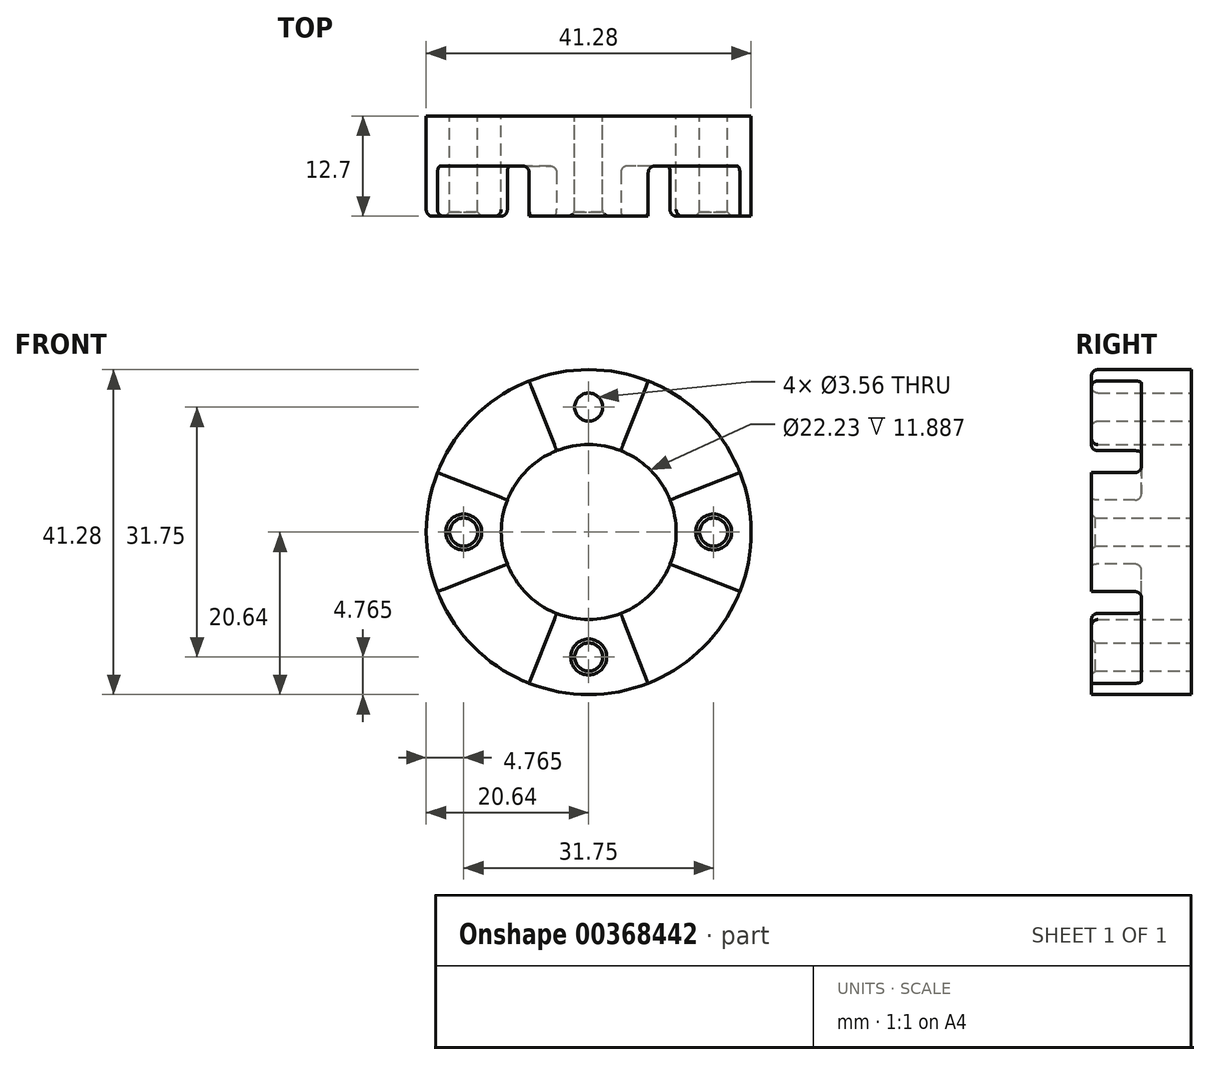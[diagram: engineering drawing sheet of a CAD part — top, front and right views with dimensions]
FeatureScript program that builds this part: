
annotation { "Feature Type Name" : "Feature", "Feature Type Description" : "" }
export const myFeature = defineFeature(function(context is Context, id is Id, definition is map)
    precondition{}
    {
        {
            var Q0;
            Q0=qCreatedBy(makeId("Front.planeOp"),FACE);
            var sketch = newSketch(context, id + "F0", { "sketchPlane" : qUnion([Q0]), "disableImprinting" : false});
            skCircle(sketch, "E0", {"center": v(0, 0) * mm, "radius": 20.64 * mm});
            skCircle(sketch, "E1", {"center": v(0, 0) * mm, "radius": 11.11 * mm});
            skLineSegment(sketch, "E2", {"start": v(0, 20.64) * mm, "end": v(0, -40.4) * mm, "construction": true});
            skLineSegment(sketch, "E3", {"start": v(-50.78, 0) * mm, "end": v(44.22, 0) * mm, "construction": true});
            skCircle(sketch, "E4", {"center": v(0, 15.88) * mm, "radius": 1.78 * mm});
            skPoint(sketch, "E5.orphan", {"position": v(0, 46.95) * mm});
            skCircle(sketch, "E6.1.0", {"center": v(-15.88, 0) * mm, "radius": 1.78 * mm});
            skCircle(sketch, "E6.2.0", {"center": v(0, -15.88) * mm, "radius": 1.78 * mm});
            skCircle(sketch, "E6.3.0", {"center": v(15.88, 0) * mm, "radius": 1.78 * mm});
            skSolve(sketch);
        }
        {
            var Q0;
            Q0=makeQuery(id+"F0.imprint","IMPRINT",FACE,{"disambiguationData":[TD([[makeQuery(id+"F0.imprint","IMPRINT",EDGE,{"derivedFrom":sQuery(id+"F0.wireOp",EDGE,"E0")}),1.0]])]});
            extrude(context, id + "F1", {"entities" : qUnion([Q0]), "flatOperationType" : FlatOperationType.REMOVE, "offsetDistance" : 25.4 * mm, "depth" : 12.7 * mm, "domain" : OperationDomain.MODEL});
        }
        {
            var Q0;
            Q0=makeQuery(id+"F1.opExtrude","CAP_EDGE",EDGE,{"disambiguationData":[OSD([sQuery(id+"F0.wireOp",EDGE,"E6.1.0")])],"isStart":false});
            var Q1;
            Q1=makeQuery(id+"F1.opExtrude","CAP_EDGE",EDGE,{"disambiguationData":[OSD([sQuery(id+"F0.wireOp",EDGE,"E4")])],"isStart":false});
            var Q2;
            Q2=makeQuery(id+"F1.opExtrude","CAP_EDGE",EDGE,{"disambiguationData":[OSD([sQuery(id+"F0.wireOp",EDGE,"E6.3.0")])],"isStart":false});
            var Q3;
            Q3=makeQuery(id+"F1.opExtrude","CAP_EDGE",EDGE,{"disambiguationData":[OSD([sQuery(id+"F0.wireOp",EDGE,"E6.2.0")])],"isStart":false});
            chamfer(context, id + "F2", {"entities" : qUnion([Q0, Q1, Q2, Q3]), "width" : 0.5 * mm, "tangentPropagation" : true});
        }
        {
            var Q0;
            Q0=makeQuery(id+"F1.opExtrude","CAP_FACE",FACE,{"disambiguationData":[OSD([sQuery(id+"F0.wireOp",EDGE,"E0"),sQuery(id+"F0.wireOp",EDGE,"E1"),sQuery(id+"F0.wireOp",EDGE,"E4"),sQuery(id+"F0.wireOp",EDGE,"E6.1.0"),sQuery(id+"F0.wireOp",EDGE,"E6.2.0"),sQuery(id+"F0.wireOp",EDGE,"E6.3.0")])],"isStart":false});
            var sketch = newSketch(context, id + "F3", { "sketchPlane" : qUnion([Q0]), "disableImprinting" : false});
            skLineSegment(sketch, "E7", {"start": v(19.2, 7.56) * mm, "end": v(0, 0) * mm});
            skLineSegment(sketch, "E8", {"start": v(19.2, -7.56) * mm, "end": v(0, 0) * mm});
            skLineSegment(sketch, "E9", {"start": v(7.56, 19.2) * mm, "end": v(0, 0) * mm});
            skLineSegment(sketch, "E10", {"start": v(0, 0) * mm, "end": v(7.56, -19.2) * mm});
            skLineSegment(sketch, "E11", {"start": v(0, 0) * mm, "end": v(-7.56, -19.2) * mm});
            skLineSegment(sketch, "E12", {"start": v(0, 0) * mm, "end": v(-19.2, -7.56) * mm});
            skLineSegment(sketch, "E13", {"start": v(0, 0) * mm, "end": v(-19.2, 7.56) * mm});
            skLineSegment(sketch, "E14", {"start": v(0, 0) * mm, "end": v(-7.56, 19.2) * mm});
            skSolve(sketch);
        }
        {
            var Q0;
            {var subQ0=sQuery(id+"F3.wireOp",EDGE,"E7");var subQ1=makeQuery(id+"F1.opExtrude","CAP_EDGE",EDGE,{"disambiguationData":[OSD([sQuery(id+"F0.wireOp",EDGE,"E0")])],"isStart":false});var subQ2=makeQuery(id+"F3.imprint","INTERSECT",VERTEX,{"derivedFrom":[subQ1,subQ0]});Q0=makeQuery(id+"F3.imprint","IMPRINT",FACE,{"disambiguationData":[TD([[makeQuery(id+"F3.imprint","IMPRINT",EDGE,{"disambiguationData":[TD([[subQ2,-1.0]])],"derivedFrom":subQ0}),-1.0]])]});}
            var Q1;
            {var subQ0=sQuery(id+"F3.wireOp",EDGE,"E8");var subQ1=makeQuery(id+"F1.opExtrude","CAP_EDGE",EDGE,{"disambiguationData":[OSD([sQuery(id+"F0.wireOp",EDGE,"E0")])],"isStart":false});var subQ2=makeQuery(id+"F3.imprint","INTERSECT",VERTEX,{"derivedFrom":[subQ1,subQ0]});Q1=makeQuery(id+"F3.imprint","IMPRINT",FACE,{"disambiguationData":[TD([[makeQuery(id+"F3.imprint","IMPRINT",EDGE,{"disambiguationData":[TD([[subQ2,-1.0]])],"derivedFrom":subQ0}),1.0]])]});}
            var Q2;
            {var subQ0=sQuery(id+"F3.wireOp",EDGE,"E11");var subQ1=makeQuery(id+"F1.opExtrude","CAP_EDGE",EDGE,{"disambiguationData":[OSD([sQuery(id+"F0.wireOp",EDGE,"E0")])],"isStart":false});var subQ2=makeQuery(id+"F3.imprint","INTERSECT",VERTEX,{"derivedFrom":[subQ1,subQ0]});Q2=makeQuery(id+"F3.imprint","IMPRINT",FACE,{"disambiguationData":[TD([[makeQuery(id+"F3.imprint","IMPRINT",EDGE,{"disambiguationData":[TD([[subQ2,1.0]])],"derivedFrom":subQ0}),-1.0]])]});}
            var Q3;
            {var subQ0=sQuery(id+"F3.wireOp",EDGE,"E13");var subQ1=makeQuery(id+"F1.opExtrude","CAP_EDGE",EDGE,{"disambiguationData":[OSD([sQuery(id+"F0.wireOp",EDGE,"E0")])],"isStart":false});var subQ2=makeQuery(id+"F3.imprint","INTERSECT",VERTEX,{"derivedFrom":[subQ1,subQ0]});Q3=makeQuery(id+"F3.imprint","IMPRINT",FACE,{"disambiguationData":[TD([[makeQuery(id+"F3.imprint","IMPRINT",EDGE,{"disambiguationData":[TD([[subQ2,1.0]])],"derivedFrom":subQ0}),-1.0]])]});}
            extrude(context, id + "F4", {"entities" : qUnion([Q0, Q1, Q2, Q3]), "operationType" : NewBodyOperationType.REMOVE, "oppositeDirection" : true, "depth" : 6.35 * mm});
        }
        {
            var Q0;
            Q0=makeQuery(id+"F4.boolean.opBoolean","COPY",EDGE,{"derivedFrom":makeQuery(id+"F4.opExtrude","CAP_EDGE",EDGE,{"disambiguationData":[OSD([sQuery(id+"F3.wireOp",EDGE,"E7")])],"isStart":true})});
            var Q1;
            Q1=makeQuery(id+"F4.boolean.opBoolean","COPY",EDGE,{"derivedFrom":makeQuery(id+"F4.opExtrude","CAP_EDGE",EDGE,{"disambiguationData":[OSD([sQuery(id+"F3.wireOp",EDGE,"E7")])],"isStart":false})});
            var Q2;
            Q2=makeQuery(id+"F4.boolean.opBoolean","COPY",EDGE,{"derivedFrom":makeQuery(id+"F4.opExtrude","CAP_EDGE",EDGE,{"disambiguationData":[OSD([sQuery(id+"F3.wireOp",EDGE,"E9")])],"isStart":true})});
            var Q3;
            Q3=makeQuery(id+"F4.boolean.opBoolean","COPY",EDGE,{"derivedFrom":makeQuery(id+"F4.opExtrude","CAP_EDGE",EDGE,{"disambiguationData":[OSD([sQuery(id+"F3.wireOp",EDGE,"E8")])],"isStart":true})});
            var Q4;
            Q4=makeQuery(id+"F4.boolean.opBoolean","COPY",EDGE,{"derivedFrom":makeQuery(id+"F4.opExtrude","CAP_EDGE",EDGE,{"disambiguationData":[OSD([sQuery(id+"F3.wireOp",EDGE,"E10")])],"isStart":true})});
            var Q5;
            Q5=makeQuery(id+"F4.boolean.opBoolean","COPY",EDGE,{"derivedFrom":makeQuery(id+"F4.opExtrude","CAP_EDGE",EDGE,{"disambiguationData":[OSD([sQuery(id+"F3.wireOp",EDGE,"E10")])],"isStart":false})});
            var Q6;
            Q6=makeQuery(id+"F4.boolean.opBoolean","COPY",EDGE,{"derivedFrom":makeQuery(id+"F4.opExtrude","CAP_EDGE",EDGE,{"disambiguationData":[OSD([sQuery(id+"F3.wireOp",EDGE,"E11")])],"isStart":true})});
            var Q7;
            Q7=makeQuery(id+"F4.boolean.opBoolean","COPY",EDGE,{"derivedFrom":makeQuery(id+"F4.opExtrude","CAP_EDGE",EDGE,{"disambiguationData":[OSD([sQuery(id+"F3.wireOp",EDGE,"E13")])],"isStart":true})});
            var Q8;
            Q8=makeQuery(id+"F4.boolean.opBoolean","COPY",EDGE,{"derivedFrom":makeQuery(id+"F4.opExtrude","CAP_EDGE",EDGE,{"disambiguationData":[OSD([sQuery(id+"F3.wireOp",EDGE,"E13")])],"isStart":false})});
            var Q9;
            Q9=makeQuery(id+"F4.boolean.opBoolean","COPY",EDGE,{"derivedFrom":makeQuery(id+"F4.opExtrude","CAP_EDGE",EDGE,{"disambiguationData":[OSD([sQuery(id+"F3.wireOp",EDGE,"E14")])],"isStart":true})});
            var Q10;
            Q10=makeQuery(id+"F4.boolean.opBoolean","COPY",EDGE,{"derivedFrom":makeQuery(id+"F4.opExtrude","CAP_EDGE",EDGE,{"disambiguationData":[OSD([sQuery(id+"F3.wireOp",EDGE,"E11")])],"isStart":false})});
            var Q11;
            Q11=makeQuery(id+"F4.boolean.opBoolean","COPY",EDGE,{"derivedFrom":makeQuery(id+"F4.opExtrude","CAP_EDGE",EDGE,{"disambiguationData":[OSD([sQuery(id+"F3.wireOp",EDGE,"E8")])],"isStart":false})});
            var Q12;
            Q12=makeQuery(id+"F4.boolean.opBoolean","COPY",EDGE,{"derivedFrom":makeQuery(id+"F4.opExtrude","CAP_EDGE",EDGE,{"disambiguationData":[OSD([sQuery(id+"F3.wireOp",EDGE,"E12")])],"isStart":false})});
            var Q13;
            Q13=makeQuery(id+"F4.boolean.opBoolean","COPY",EDGE,{"derivedFrom":makeQuery(id+"F4.opExtrude","CAP_EDGE",EDGE,{"disambiguationData":[OSD([sQuery(id+"F3.wireOp",EDGE,"E12")])],"isStart":true})});
            var Q14;
            Q14=makeQuery(id+"F4.boolean.opBoolean","COPY",EDGE,{"derivedFrom":makeQuery(id+"F4.opExtrude","CAP_EDGE",EDGE,{"disambiguationData":[OSD([sQuery(id+"F3.wireOp",EDGE,"E14")])],"isStart":false})});
            var Q15;
            Q15=makeQuery(id+"F4.boolean.opBoolean","COPY",EDGE,{"derivedFrom":makeQuery(id+"F4.opExtrude","CAP_EDGE",EDGE,{"disambiguationData":[OSD([sQuery(id+"F3.wireOp",EDGE,"E9")])],"isStart":false})});
            var Q16;
            {var subQ0=sQuery(id+"F0.wireOp",EDGE,"E1");Q16=makeQuery(id+"F4.boolean.opBoolean","SPLIT",EDGE,{"disambiguationData":[TD([makeQuery(id+"F4.opExtrude","SWEPT_FACE",FACE,{"disambiguationData":[OSD([sQuery(id+"F3.wireOp",EDGE,"E7")])]})])],"derivedFrom":makeQuery(id+"F1.opExtrude","CAP_EDGE",EDGE,{"disambiguationData":[OSD([subQ0])],"isStart":false})});}
            var Q17;
            {var subQ0=sQuery(id+"F0.wireOp",EDGE,"E1");Q17=makeQuery(id+"F4.boolean.opBoolean","SPLIT",EDGE,{"disambiguationData":[TD([makeQuery(id+"F4.opExtrude","SWEPT_FACE",FACE,{"disambiguationData":[OSD([sQuery(id+"F3.wireOp",EDGE,"E10")])]})])],"derivedFrom":makeQuery(id+"F1.opExtrude","CAP_EDGE",EDGE,{"disambiguationData":[OSD([subQ0])],"isStart":false})});}
            var Q18;
            {var subQ0=sQuery(id+"F0.wireOp",EDGE,"E1");Q18=makeQuery(id+"F4.boolean.opBoolean","SPLIT",EDGE,{"disambiguationData":[TD([makeQuery(id+"F4.opExtrude","SWEPT_FACE",FACE,{"disambiguationData":[OSD([sQuery(id+"F3.wireOp",EDGE,"E12")])]})])],"derivedFrom":makeQuery(id+"F1.opExtrude","CAP_EDGE",EDGE,{"disambiguationData":[OSD([subQ0])],"isStart":false})});}
            var Q19;
            {var subQ0=sQuery(id+"F0.wireOp",EDGE,"E1");Q19=makeQuery(id+"F4.boolean.opBoolean","SPLIT",EDGE,{"disambiguationData":[TD([makeQuery(id+"F4.opExtrude","SWEPT_FACE",FACE,{"disambiguationData":[OSD([sQuery(id+"F3.wireOp",EDGE,"E9")])]})])],"derivedFrom":makeQuery(id+"F1.opExtrude","CAP_EDGE",EDGE,{"disambiguationData":[OSD([subQ0])],"isStart":false})});}
            fillet(context, id + "F5", {"entities" : qUnion([Q0, Q1, Q2, Q3, Q4, Q5, Q6, Q7, Q8, Q9, Q10, Q11, Q12, Q13, Q14, Q15, Q16, Q17, Q18, Q19]), "radius" : 0.81 * mm, "tangentPropagation" : true, "allowEdgeOverflow" : false});
        }
        {
            var Q0;
            {var subQ0=sQuery(id+"F0.wireOp",EDGE,"E0");Q0=makeQuery(id+"F4.boolean.opBoolean","SPLIT",EDGE,{"disambiguationData":[TD([makeQuery(id+"F4.opExtrude","SWEPT_FACE",FACE,{"disambiguationData":[OSD([sQuery(id+"F3.wireOp",EDGE,"E12")])]})])],"derivedFrom":makeQuery(id+"F1.opExtrude","CAP_EDGE",EDGE,{"disambiguationData":[OSD([subQ0])],"isStart":false})});}
            var Q1;
            {var subQ0=sQuery(id+"F0.wireOp",EDGE,"E0");Q1=makeQuery(id+"F4.boolean.opBoolean","SPLIT",EDGE,{"disambiguationData":[TD([makeQuery(id+"F4.opExtrude","SWEPT_FACE",FACE,{"disambiguationData":[OSD([sQuery(id+"F3.wireOp",EDGE,"E9")])]})])],"derivedFrom":makeQuery(id+"F1.opExtrude","CAP_EDGE",EDGE,{"disambiguationData":[OSD([subQ0])],"isStart":false})});}
            var Q2;
            Q2=makeQuery(id+"F2.opChamfer","BLEND_FACE",FACE,{"disambiguationData":[OSD([sQuery(id+"F0.wireOp",EDGE,"E4")])]});
            fillet(context, id + "F6", {"entities" : qUnion([Q0, Q1, Q2]), "radius" : 0.81 * mm, "tangentPropagation" : true, "allowEdgeOverflow" : false});
        }
    });
